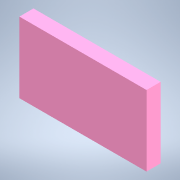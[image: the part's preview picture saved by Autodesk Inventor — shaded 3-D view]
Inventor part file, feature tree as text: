
AUTODESK INVENTOR PART (.ipt)
format: ipt  version: 2022.3 (Build 263350000, 350)  size: 98,816 bytes
history: native  units: in
note: dims shown in document units (in); Inventor stores cm internally (conversion verified against a paired STEP export)
features: extrude x1, sketch x1
ambient origin geometry x8: Origin, YZ Plane, XZ Plane, XY Plane, X Axis, Y Axis, Z Axis, Center Point
bodies: Solid1 (feature_tree)
feature tree (2):
  extrude  "Extrusion1"  Depth=4.5in
  sketch  "Sketch1"  dims[d0=0.5in d1=4.5in d2=2.5in d3=0.0in]
